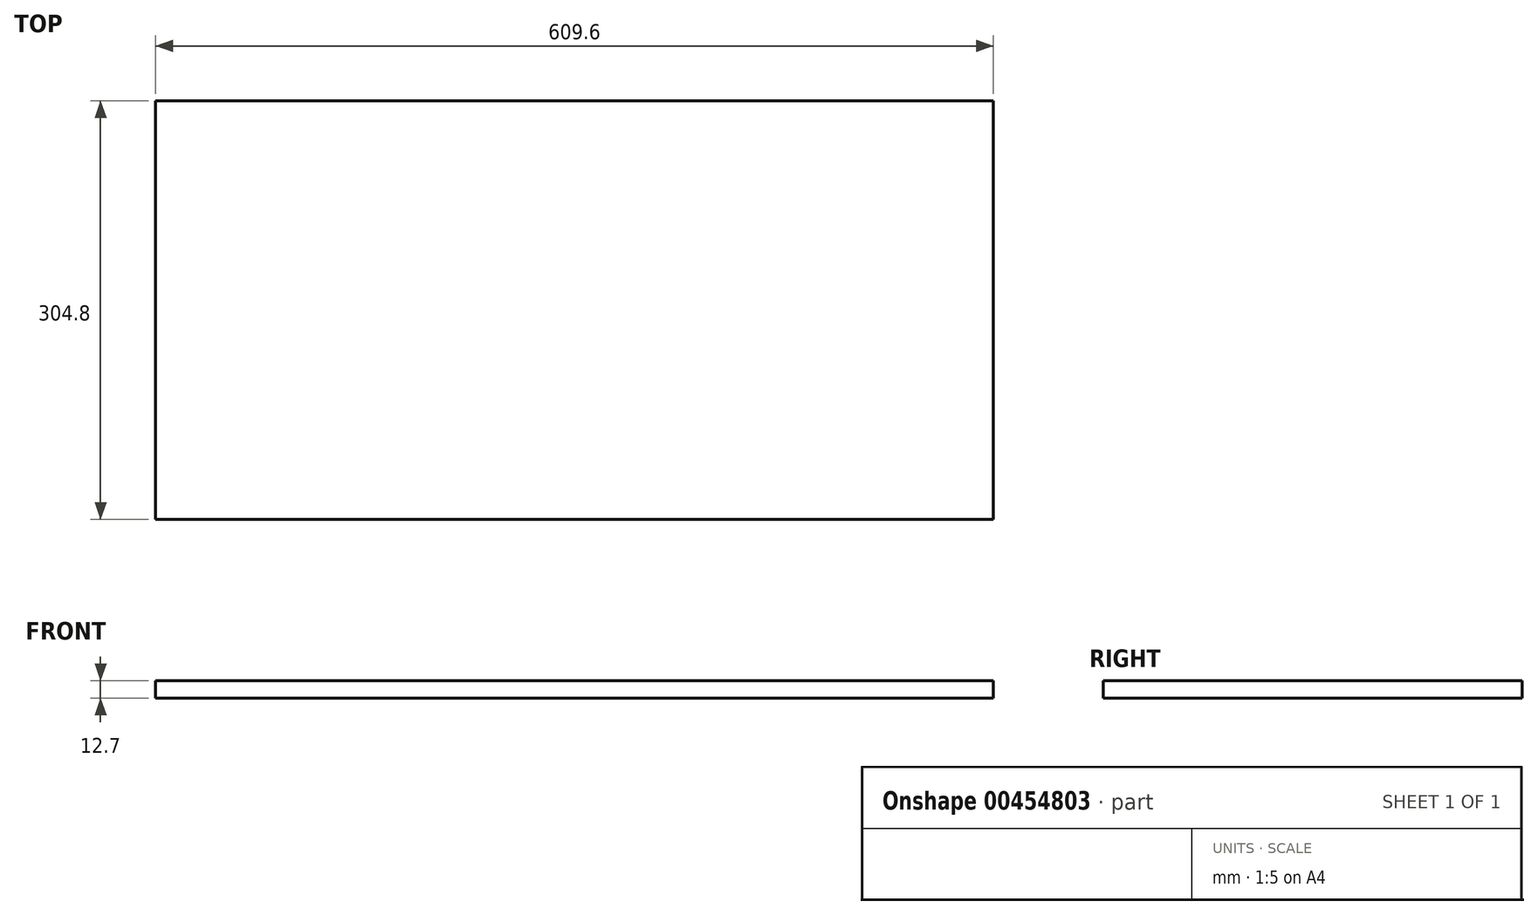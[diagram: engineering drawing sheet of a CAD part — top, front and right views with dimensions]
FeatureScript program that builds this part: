
annotation { "Feature Type Name" : "Feature", "Feature Type Description" : "" }
export const myFeature = defineFeature(function(context is Context, id is Id, definition is map)
    precondition{}
    {
        {
            var Q0;
            Q0=qCreatedBy(makeId("Top.planeOp"),FACE);
            var sketch = newSketch(context, id + "F0", { "sketchPlane" : qUnion([Q0])});
            skLineSegment(sketch, "E0.bottom", {"start": v(-106.36, -138.75) * mm, "end": v(503.24, -138.75) * mm});
            skLineSegment(sketch, "E0.top", {"start": v(-106.36, 166.05) * mm, "end": v(503.24, 166.05) * mm});
            skLineSegment(sketch, "E0.left", {"start": v(-106.36, -138.75) * mm, "end": v(-106.36, 166.05) * mm});
            skLineSegment(sketch, "E0.right", {"start": v(503.24, -138.75) * mm, "end": v(503.24, 166.05) * mm});
            skSolve(sketch);
        }
        {
            var Q0;
            Q0 = qSketchRegion(id + "F0", true);
            extrude(context, id + "F1", {"entities" : qUnion([Q0]), "depth" : 12.7 * mm});
        }
    });
